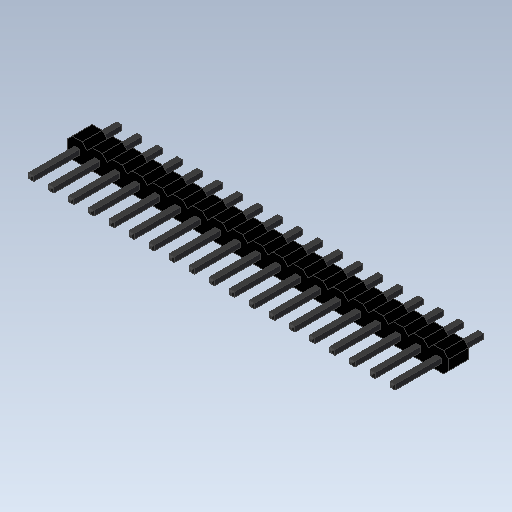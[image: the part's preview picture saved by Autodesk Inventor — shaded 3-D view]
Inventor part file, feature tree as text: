
AUTODESK INVENTOR PART (.ipt)
format: ipt  version: 2020 (Build 240168000, 168)  size: 347,648 bytes
history: imported  units: in
note: dims shown in document units (in); Inventor stores cm internally (conversion verified against a paired STEP export)
features: imported_body x1
ambient origin geometry x8: Origin, YZ Plane, XZ Plane, XY Plane, X Axis, Y Axis, Z Axis, Center Point
bodies: Solid1 (imported_parasolid), Body2 (imported_parasolid)
feature tree (1):
  imported_body  NMx_Import_Brep_tag  [imported B-rep: ~460 faces, bbox_mm=[48.26, 2.54, 11.54]]
